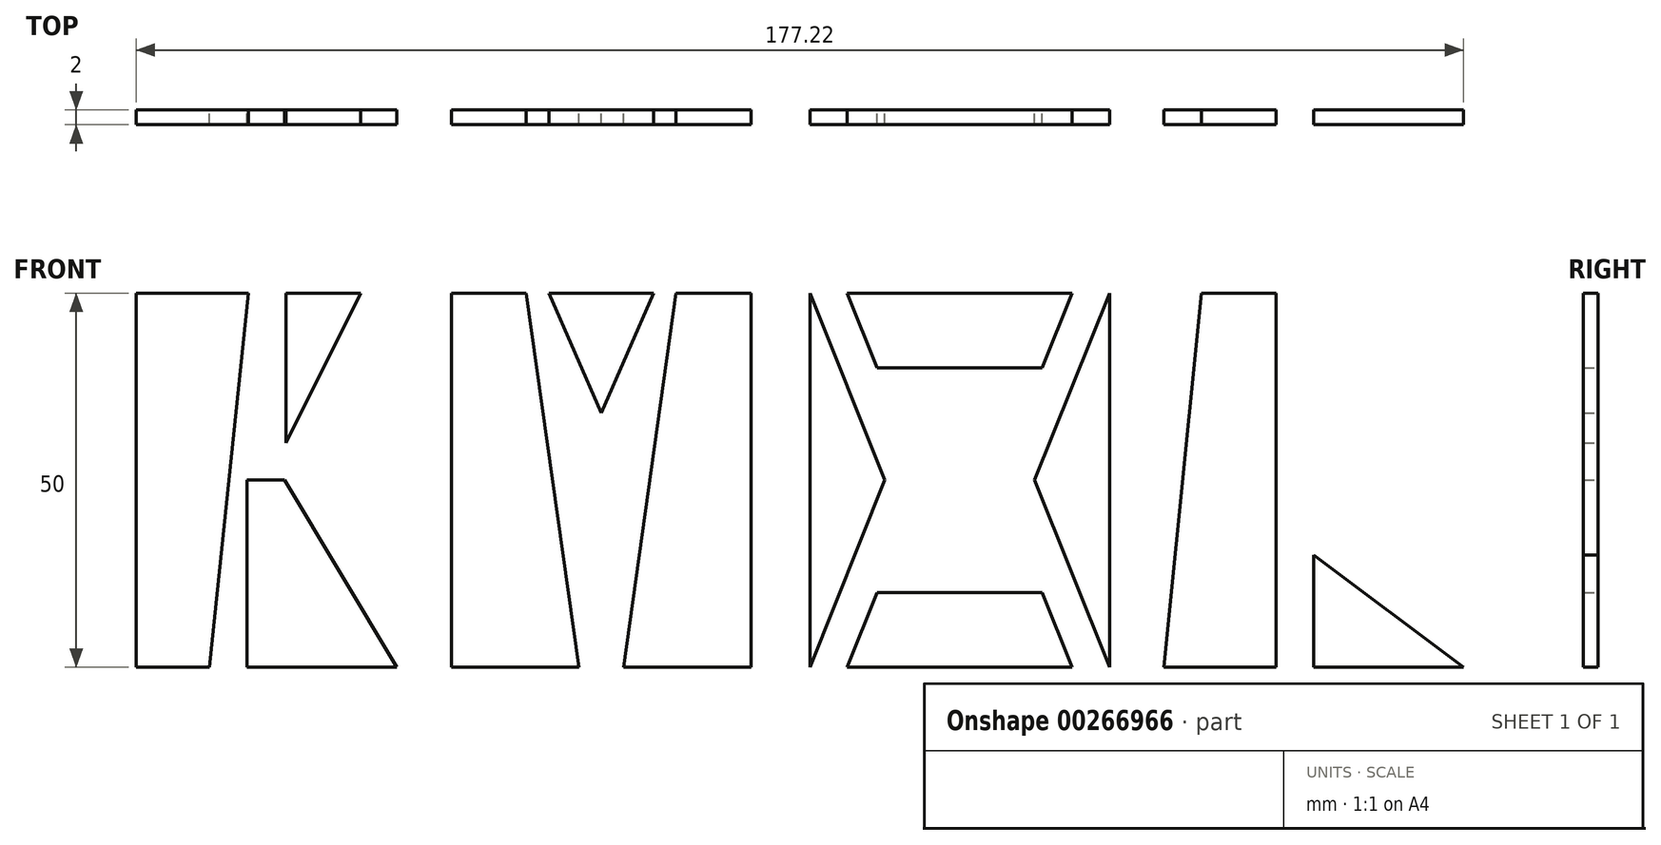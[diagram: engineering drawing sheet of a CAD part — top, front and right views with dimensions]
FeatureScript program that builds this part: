
annotation { "Feature Type Name" : "Feature", "Feature Type Description" : "" }
export const myFeature = defineFeature(function(context is Context, id is Id, definition is map)
    precondition{}
    {
        {
            var Q0;
            Q0=qCreatedBy(makeId("Front.planeOp"),FACE);
            var sketch = newSketch(context, id + "F0", { "sketchPlane" : qUnion([Q0])});
            skLineSegment(sketch, "E0", {"start": v(-55.1, 0) * mm, "end": v(-55.1, 50) * mm});
            skLineSegment(sketch, "E1", {"start": v(-55.1, 50) * mm, "end": v(-40.1, 50) * mm});
            skLineSegment(sketch, "E2", {"start": v(-40.1, 50) * mm, "end": v(-45.31, 0) * mm});
            skLineSegment(sketch, "E3", {"start": v(-45.31, 0) * mm, "end": v(-55.1, 0) * mm});
            skLineSegment(sketch, "E4", {"start": v(-40.31, 0) * mm, "end": v(-40.31, 25) * mm});
            skLineSegment(sketch, "E5", {"start": v(-40.31, 25) * mm, "end": v(-35.31, 25) * mm});
            skLineSegment(sketch, "E6", {"start": v(-35.31, 25) * mm, "end": v(-20.31, 0) * mm});
            skLineSegment(sketch, "E7", {"start": v(-20.31, 0) * mm, "end": v(-40.31, 0) * mm});
            skLineSegment(sketch, "E8", {"start": v(-35.1, 30) * mm, "end": v(-35.1, 50) * mm});
            skLineSegment(sketch, "E9", {"start": v(-35.1, 50) * mm, "end": v(-25.1, 50) * mm});
            skLineSegment(sketch, "E10", {"start": v(-25.1, 50) * mm, "end": v(-35.1, 30) * mm});
            skSolve(sketch);
        }
        {
            var Q0;
            Q0=qCreatedBy(makeId("Front.planeOp"),FACE);
            var sketch = newSketch(context, id + "F1", { "sketchPlane" : qUnion([Q0])});
            skLineSegment(sketch, "E11", {"start": v(-13, 0) * mm, "end": v(-13, 50) * mm});
            skLineSegment(sketch, "E12", {"start": v(-13, 50) * mm, "end": v(-3, 50) * mm});
            skLineSegment(sketch, "E13", {"start": v(-3, 50) * mm, "end": v(4, 0) * mm});
            skLineSegment(sketch, "E14", {"start": v(4, 0) * mm, "end": v(-13, 0) * mm});
            skLineSegment(sketch, "E15", {"start": v(0, 50) * mm, "end": v(7, 34) * mm});
            skLineSegment(sketch, "E16", {"start": v(7, 34) * mm, "end": v(14, 50) * mm});
            skLineSegment(sketch, "E17", {"start": v(14, 50) * mm, "end": v(0, 50) * mm});
            skLineSegment(sketch, "E18.MirrorCS", {"start": v(27, 50) * mm, "end": v(17, 50) * mm});
            skLineSegment(sketch, "E19.MirrorCS", {"start": v(27, 0) * mm, "end": v(27, 50) * mm});
            skLineSegment(sketch, "E20.MirrorCS", {"start": v(17, 50) * mm, "end": v(10, 0) * mm});
            skLineSegment(sketch, "E21.MirrorCS", {"start": v(10, 0) * mm, "end": v(27, 0) * mm});
            skSolve(sketch);
        }
        {
            var Q0;
            Q0=qCreatedBy(makeId("Front.planeOp"),FACE);
            var sketch = newSketch(context, id + "F2", { "sketchPlane" : qUnion([Q0])});
            skLineSegment(sketch, "E22", {"start": v(34.85, 0) * mm, "end": v(34.85, 50) * mm});
            skLineSegment(sketch, "E23", {"start": v(34.85, 50) * mm, "end": v(44.85, 25) * mm});
            skLineSegment(sketch, "E24", {"start": v(44.85, 25) * mm, "end": v(34.85, 0) * mm});
            skLineSegment(sketch, "E25", {"start": v(39.85, 0) * mm, "end": v(43.85, 10) * mm});
            skLineSegment(sketch, "E26", {"start": v(43.85, 10) * mm, "end": v(65.85, 10) * mm});
            skLineSegment(sketch, "E27", {"start": v(65.85, 10) * mm, "end": v(69.85, 0) * mm});
            skLineSegment(sketch, "E28", {"start": v(69.85, 0) * mm, "end": v(39.85, 0) * mm});
            skLineSegment(sketch, "E29.MirrorCS", {"start": v(74.85, 50) * mm, "end": v(64.85, 25) * mm});
            skLineSegment(sketch, "E30.MirrorCS", {"start": v(74.85, 0) * mm, "end": v(74.85, 50) * mm});
            skLineSegment(sketch, "E31.MirrorCS", {"start": v(64.85, 25) * mm, "end": v(74.85, 0) * mm});
            skLineSegment(sketch, "E32.MirrorCS", {"start": v(43.85, 40) * mm, "end": v(65.85, 40) * mm});
            skLineSegment(sketch, "E33.MirrorCS", {"start": v(69.85, 50) * mm, "end": v(39.85, 50) * mm});
            skLineSegment(sketch, "E34.MirrorCS", {"start": v(39.85, 50) * mm, "end": v(43.85, 40) * mm});
            skLineSegment(sketch, "E35.MirrorCS", {"start": v(65.85, 40) * mm, "end": v(69.85, 50) * mm});
            skSolve(sketch);
        }
        {
            var Q0;
            Q0=qCreatedBy(makeId("Front.planeOp"),FACE);
            var sketch = newSketch(context, id + "F3", { "sketchPlane" : qUnion([Q0])});
            skLineSegment(sketch, "E36", {"start": v(82.12, 0) * mm, "end": v(87.12, 50) * mm});
            skLineSegment(sketch, "E37", {"start": v(87.12, 50) * mm, "end": v(97.12, 50) * mm});
            skLineSegment(sketch, "E38", {"start": v(97.12, 50) * mm, "end": v(97.12, 0) * mm});
            skLineSegment(sketch, "E39", {"start": v(97.12, 0) * mm, "end": v(82.12, 0) * mm});
            skLineSegment(sketch, "E40", {"start": v(102.12, 0) * mm, "end": v(102.12, 15) * mm});
            skLineSegment(sketch, "E41", {"start": v(102.12, 15) * mm, "end": v(122.12, 0) * mm});
            skLineSegment(sketch, "E42", {"start": v(122.12, 0) * mm, "end": v(102.12, 0) * mm});
            skSolve(sketch);
        }
        {
            var Q0;
            Q0 = qSketchRegion(id + "F0", true);
            var Q1;
            Q1 = qSketchRegion(id + "F1", true);
            var Q2;
            Q2 = qSketchRegion(id + "F2", true);
            var Q3;
            Q3 = qSketchRegion(id + "F3", true);
            extrude(context, id + "F4", {"entities" : qUnion([Q0, Q1, Q2, Q3]), "depth" : 2 * mm});
        }
    });
